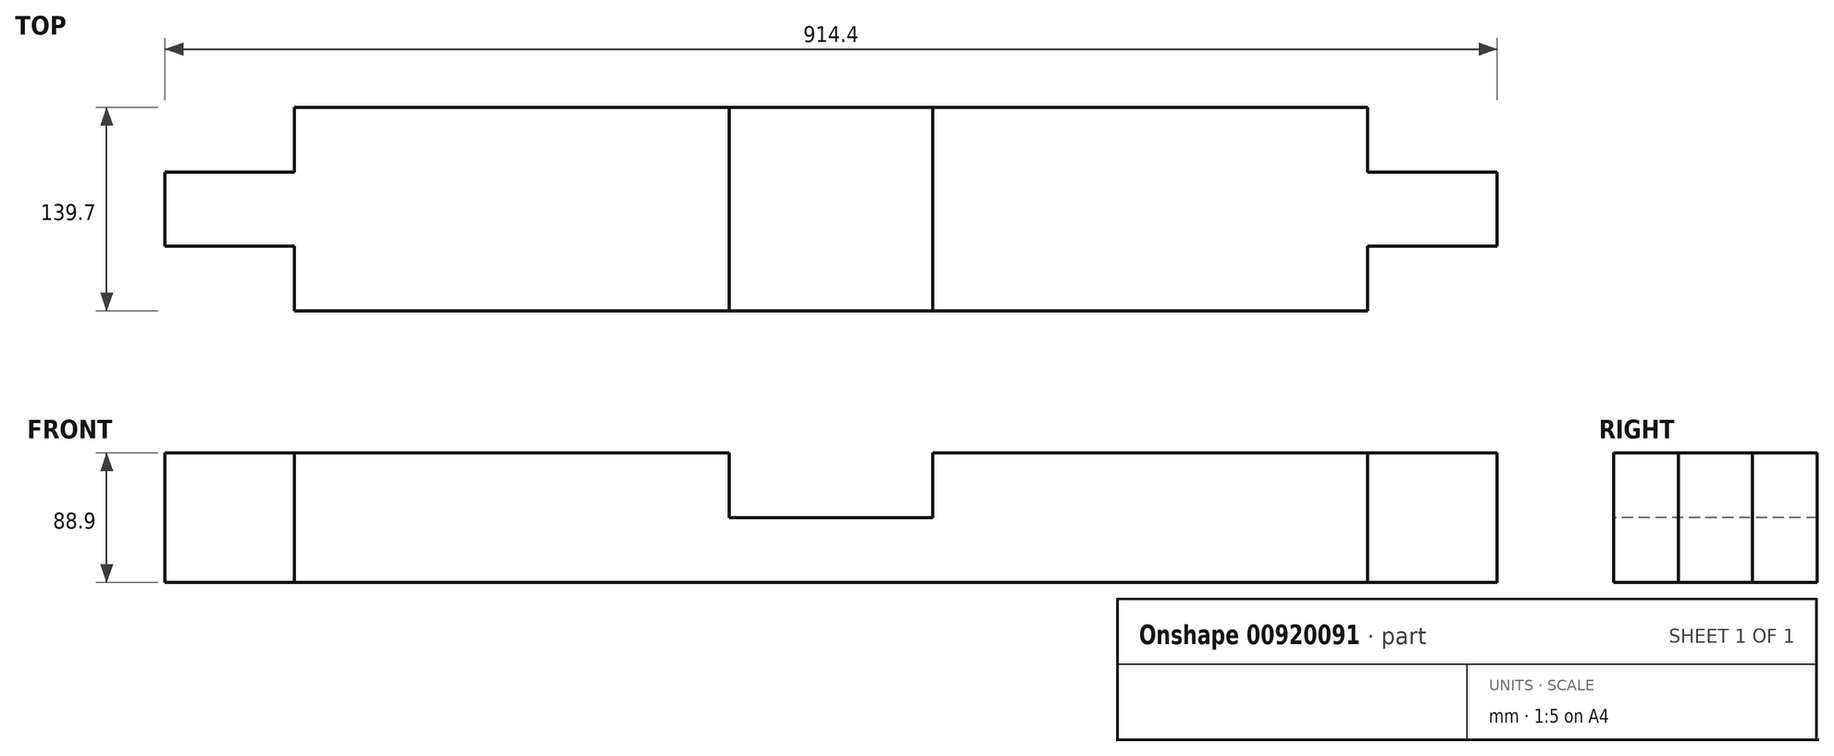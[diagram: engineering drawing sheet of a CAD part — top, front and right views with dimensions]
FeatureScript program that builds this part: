
annotation { "Feature Type Name" : "Feature", "Feature Type Description" : "" }
export const myFeature = defineFeature(function(context is Context, id is Id, definition is map)
    precondition{}
    {
        {
            var Q0;
            Q0=qCreatedBy(makeId("Top.planeOp"),FACE);
            var sketch = newSketch(context, id + "F0", { "sketchPlane" : qUnion([Q0])});
            skLineSegment(sketch, "E0.bottom", {"start": v(0, 0) * mm, "end": v(914.4, 0) * mm});
            skLineSegment(sketch, "E0.top", {"start": v(0, 139.7) * mm, "end": v(914.4, 139.7) * mm});
            skLineSegment(sketch, "E0.left", {"start": v(0, 0) * mm, "end": v(0, 139.7) * mm});
            skLineSegment(sketch, "E0.right", {"start": v(914.4, 0) * mm, "end": v(914.4, 139.7) * mm});
            skSolve(sketch);
        }
        {
            var Q0;
            Q0=makeQuery(id+"F0.imprint","IMPRINT",FACE,{"disambiguationData":[TD([[makeQuery(id+"F0.imprint","IMPRINT",EDGE,{"derivedFrom":sQuery(id+"F0.wireOp",EDGE,"E0.bottom")}),1.0]])]});
            extrude(context, id + "F1", {"entities" : qUnion([Q0]), "depth" : 88.9 * mm, "offsetDistance" : 25.4 * mm});
        }
        {
            var Q0;
            Q0=makeQuery(id+"F1.opExtrude","CAP_FACE",FACE,{"disambiguationData":[OSD([sQuery(id+"F0.wireOp",EDGE,"E0.bottom"),sQuery(id+"F0.wireOp",EDGE,"E0.top"),sQuery(id+"F0.wireOp",EDGE,"E0.left"),sQuery(id+"F0.wireOp",EDGE,"E0.right")])],"isStart":false});
            var sketch = newSketch(context, id + "F2", { "sketchPlane" : qUnion([Q0])});
            skLineSegment(sketch, "E1.bottom", {"start": v(0, 139.7) * mm, "end": v(88.9, 139.7) * mm});
            skLineSegment(sketch, "E1.top", {"start": v(0, 95.25) * mm, "end": v(88.9, 95.25) * mm});
            skLineSegment(sketch, "E1.left", {"start": v(0, 139.7) * mm, "end": v(0, 95.25) * mm});
            skLineSegment(sketch, "E1.right", {"start": v(88.9, 139.7) * mm, "end": v(88.9, 95.25) * mm});
            skLineSegment(sketch, "E2.bottom", {"start": v(0, 0) * mm, "end": v(88.9, 0) * mm});
            skLineSegment(sketch, "E2.top", {"start": v(0, 44.45) * mm, "end": v(88.9, 44.45) * mm});
            skLineSegment(sketch, "E2.left", {"start": v(0, 0) * mm, "end": v(0, 44.45) * mm});
            skLineSegment(sketch, "E2.right", {"start": v(88.9, 0) * mm, "end": v(88.9, 44.45) * mm});
            skLineSegment(sketch, "E3", {"start": v(457.2, 139.7) * mm, "end": v(457.2, 0) * mm, "construction": true});
            skLineSegment(sketch, "E4.MirrorCS", {"start": v(914.4, 139.7) * mm, "end": v(914.4, 95.25) * mm});
            skLineSegment(sketch, "E5.MirrorCS", {"start": v(914.4, 139.7) * mm, "end": v(825.5, 139.7) * mm});
            skLineSegment(sketch, "E6.MirrorCS", {"start": v(825.5, 139.7) * mm, "end": v(825.5, 95.25) * mm});
            skLineSegment(sketch, "E7.MirrorCS", {"start": v(914.4, 0) * mm, "end": v(914.4, 44.45) * mm});
            skLineSegment(sketch, "E8.MirrorCS", {"start": v(914.4, 44.45) * mm, "end": v(825.5, 44.45) * mm});
            skLineSegment(sketch, "E9.MirrorCS", {"start": v(914.4, 0) * mm, "end": v(825.5, 0) * mm});
            skLineSegment(sketch, "E10.MirrorCS", {"start": v(914.4, 95.25) * mm, "end": v(825.5, 95.25) * mm});
            skLineSegment(sketch, "E11.MirrorCS", {"start": v(825.5, 0) * mm, "end": v(825.5, 44.45) * mm});
            skSolve(sketch);
        }
        {
            var Q0;
            Q0 = qSketchRegion(id + "F2", true);
            extrude(context, id + "F3", {"entities" : qUnion([Q0]), "operationType" : NewBodyOperationType.REMOVE, "endBound" : BoundingType.UP_TO_NEXT, "oppositeDirection" : true, "depth" : 25.4 * mm, "offsetDistance" : 25.4 * mm});
        }
        {
            var Q0;
            Q0=makeQuery(id+"F1.opExtrude","SWEPT_FACE",FACE,{"disambiguationData":[OSD([sQuery(id+"F0.wireOp",EDGE,"E0.bottom")])]});
            var sketch = newSketch(context, id + "F4", { "sketchPlane" : qUnion([Q0])});
            skLineSegment(sketch, "E12.bottom", {"start": v(387.35, 88.9) * mm, "end": v(527.05, 88.9) * mm});
            skLineSegment(sketch, "E12.top", {"start": v(387.35, 44.45) * mm, "end": v(527.05, 44.45) * mm});
            skLineSegment(sketch, "E12.left", {"start": v(387.35, 88.9) * mm, "end": v(387.35, 44.45) * mm});
            skLineSegment(sketch, "E12.right", {"start": v(527.05, 88.9) * mm, "end": v(527.05, 44.45) * mm});
            skSolve(sketch);
        }
        {
            var Q0;
            Q0 = qSketchRegion(id + "F4", true);
            extrude(context, id + "F5", {"entities" : qUnion([Q0]), "operationType" : NewBodyOperationType.REMOVE, "endBound" : BoundingType.UP_TO_NEXT, "oppositeDirection" : true, "depth" : 25.4 * mm, "offsetDistance" : 25.4 * mm});
        }
    });
